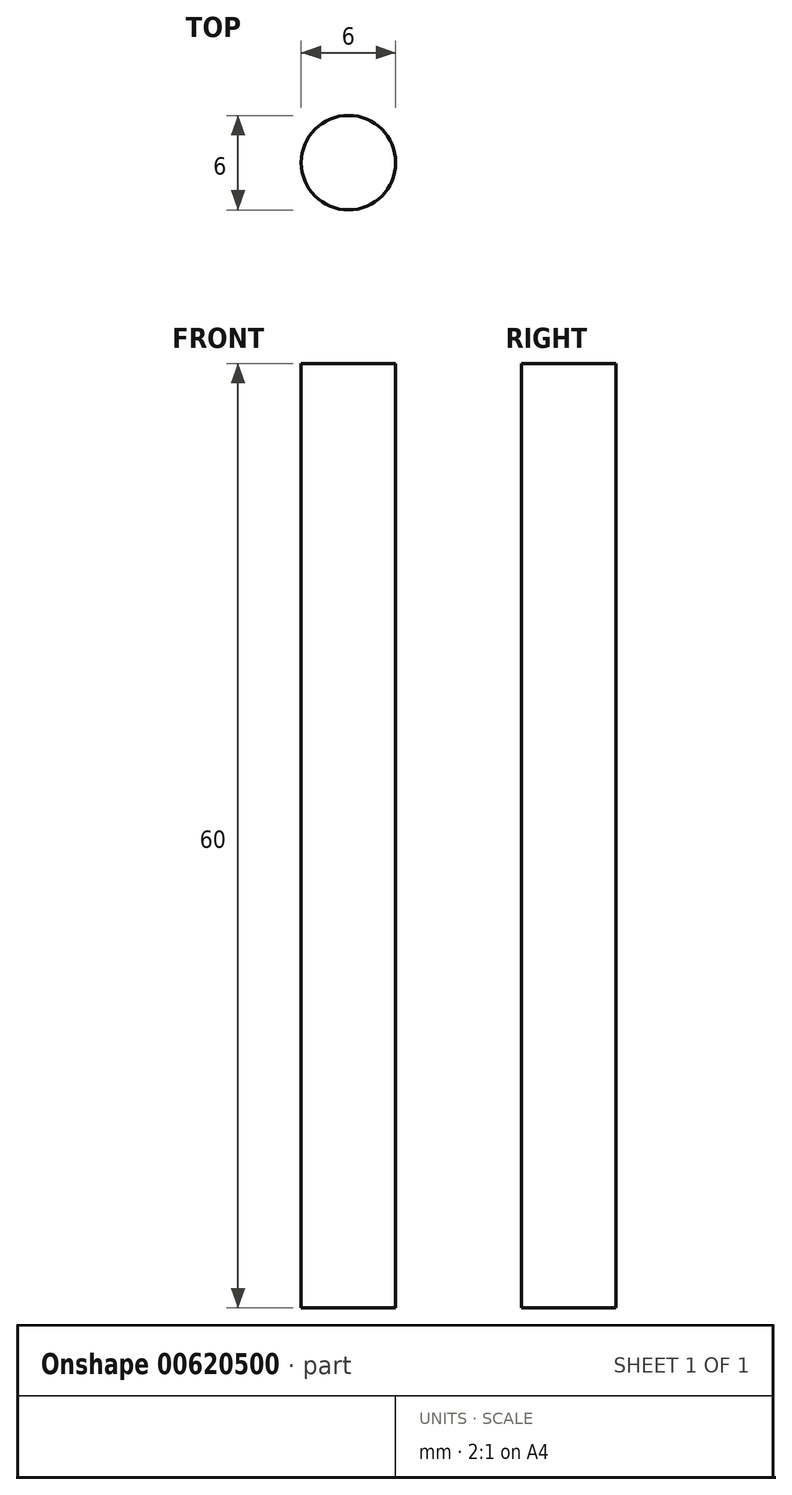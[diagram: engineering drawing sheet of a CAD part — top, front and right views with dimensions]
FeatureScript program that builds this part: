
annotation { "Feature Type Name" : "Feature", "Feature Type Description" : "" }
export const myFeature = defineFeature(function(context is Context, id is Id, definition is map)
    precondition{}
    {
        {
            var Q0;
            Q0=qCreatedBy(makeId("Top.planeOp"),FACE);
            var sketch = newSketch(context, id + "F0", { "sketchPlane" : qUnion([Q0])});
            skCircle(sketch, "E0", {"center": v(-15.04, 8.5) * mm, "radius": 3 * mm});
            skSolve(sketch);
        }
        {
            var Q0;
            Q0=sQuery(id+"F0.wireOp",EDGE,"E0");
            extrude(context, id + "F1", {"bodyType" : ToolBodyType.SURFACE, "surfaceEntities" : qUnion([Q0]), "depth" : 60 * mm, "offsetDistance" : 25 * mm});
        }
    });
